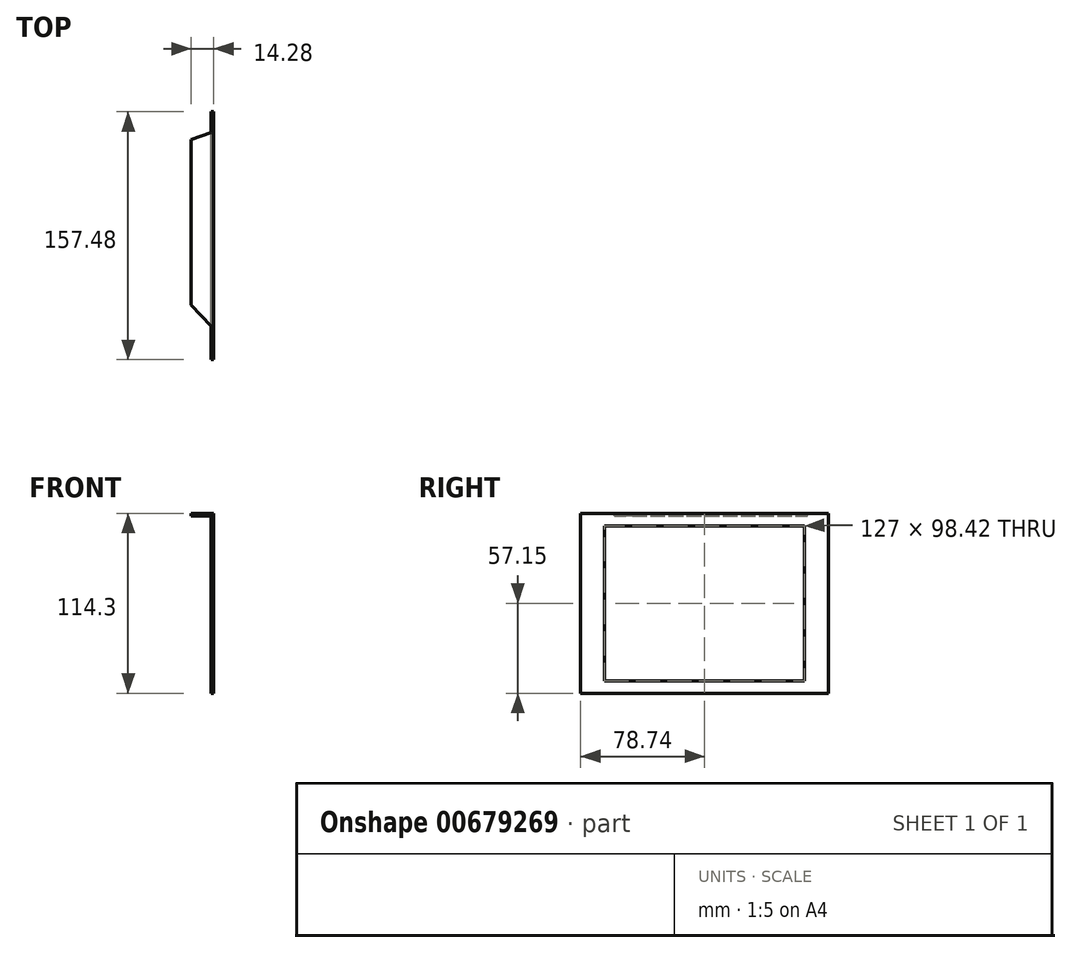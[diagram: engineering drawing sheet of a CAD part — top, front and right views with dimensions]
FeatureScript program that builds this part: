
annotation { "Feature Type Name" : "Feature", "Feature Type Description" : "" }
export const myFeature = defineFeature(function(context is Context, id is Id, definition is map)
    precondition{}
    {
        {
            var Q0;
            Q0=qCreatedBy(makeId("Top.planeOp"),FACE);
            var sketch = newSketch(context, id + "F0", { "sketchPlane" : qUnion([Q0])});
            skLineSegment(sketch, "E0.bottom", {"start": v(0.8, -78.74) * mm, "end": v(-0.8, -78.74) * mm});
            skLineSegment(sketch, "E0.top", {"start": v(0.8, 78.74) * mm, "end": v(-0.8, 78.74) * mm});
            skLineSegment(sketch, "E0.left", {"start": v(0.8, -78.74) * mm, "end": v(0.8, 78.74) * mm});
            skLineSegment(sketch, "E0.right", {"start": v(-0.8, -78.74) * mm, "end": v(-0.8, 78.74) * mm});
            skPoint(sketch, "E0.middle", {"position": v(0, 0) * mm});
            skSolve(sketch);
        }
        {
            var Q0;
            Q0=qSketchRegion(id+"F0",true);
            extrude(context, id + "F1", {"entities" : qUnion([Q0]), "depth" : 114.3 * mm});
        }
        {
            var Q0;
            Q0=makeQuery(id+"F1.opExtrude","SWEPT_FACE",FACE,{"disambiguationData":[OSD([sQuery(id+"F0.wireOp",EDGE,"E0.left")])]});
            var sketch = newSketch(context, id + "F2", { "sketchPlane" : qUnion([Q0])});
            skLineSegment(sketch, "E1.bottom", {"start": v(63.5, 106.36) * mm, "end": v(-63.5, 106.36) * mm});
            skLineSegment(sketch, "E1.top", {"start": v(63.5, 7.94) * mm, "end": v(-63.5, 7.94) * mm});
            skLineSegment(sketch, "E1.left", {"start": v(63.5, 106.36) * mm, "end": v(63.5, 7.94) * mm});
            skLineSegment(sketch, "E1.right", {"start": v(-63.5, 106.36) * mm, "end": v(-63.5, 7.94) * mm});
            skPoint(sketch, "E1.middle", {"position": v(0, 57.15) * mm});
            skPoint(sketch, "E1.middle.positionSnap0", {"position": v(-78.74, 57.15) * mm});
            skPoint(sketch, "E1.centerSnap0", {"position": v(-78.74, 57.15) * mm});
            skSolve(sketch);
        }
        {
            var Q0;
            Q0=qSketchRegion(id+"F2",true);
            extrude(context, id + "F3", {"entities" : qUnion([Q0]), "operationType" : NewBodyOperationType.REMOVE, "oppositeDirection" : true, "depth" : 25.4 * mm});
        }
        {
            var Q0;
            Q0=makeQuery(id+"F1.opExtrude","SWEPT_FACE",FACE,{"disambiguationData":[OSD([sQuery(id+"F0.wireOp",EDGE,"E0.right")])]});
            var sketch = newSketch(context, id + "F4", { "sketchPlane" : qUnion([Q0])});
            skPoint(sketch, "E2", {"position": v(-62.82, 114.3) * mm});
            skLineSegment(sketch, "E3.bottom", {"start": v(-62.82, 114.3) * mm, "end": v(54.93, 114.3) * mm});
            skLineSegment(sketch, "E3.top", {"start": v(-62.82, 112.71) * mm, "end": v(54.93, 112.71) * mm});
            skLineSegment(sketch, "E4.bottom", {"start": v(-62.82, 112.71) * mm, "end": v(-65.4, 112.71) * mm});
            skLineSegment(sketch, "E4.top", {"start": v(-62.82, 114.3) * mm, "end": v(-65.4, 114.3) * mm});
            skLineSegment(sketch, "E5.right", {"start": v(-65.4, 112.71) * mm, "end": v(-65.4, 114.3) * mm});
            skLineSegment(sketch, "E6.bottom", {"start": v(54.93, 112.71) * mm, "end": v(57.46, 112.71) * mm});
            skLineSegment(sketch, "E6.top", {"start": v(54.93, 114.3) * mm, "end": v(57.46, 114.3) * mm});
            skLineSegment(sketch, "E6.right", {"start": v(57.46, 112.71) * mm, "end": v(57.46, 114.3) * mm});
            skSolve(sketch);
        }
        {
            var Q0;
            Q0=qSketchRegion(id+"F4",true);
            extrude(context, id + "F5", {"entities" : qUnion([Q0]), "operationType" : NewBodyOperationType.ADD, "depth" : 12.7 * mm, "offsetDistance" : 25.4 * mm});
        }
        {
            var Q0;
            Q0=makeQuery(id+"F5.boolean.opBoolean","MERGE",FACE,{"derivedFrom":[makeQuery(id+"F1.opExtrude","CAP_FACE",FACE,{"disambiguationData":[OSD([sQuery(id+"F0.wireOp",EDGE,"E0.bottom"),sQuery(id+"F0.wireOp",EDGE,"E0.top"),sQuery(id+"F0.wireOp",EDGE,"E0.left"),sQuery(id+"F0.wireOp",EDGE,"E0.right")])],"isStart":false}),makeQuery(id+"F5.opExtrude","SWEPT_FACE",FACE,{"disambiguationData":[OSD([sQuery(id+"F4.wireOp",EDGE,"E3.bottom"),sQuery(id+"F4.wireOp",EDGE,"E4.top"),sQuery(id+"F4.wireOp",EDGE,"E6.top")])]})]});
            var sketch = newSketch(context, id + "F6", { "sketchPlane" : qUnion([Q0])});
            skLineSegment(sketch, "E7", {"start": v(-13.5, 65.4) * mm, "end": v(-0.8, 65.4) * mm});
            skLineSegment(sketch, "E8", {"start": v(-0.8, 65.4) * mm, "end": v(-13.5, 60.95) * mm});
            skLineSegment(sketch, "E9", {"start": v(-13.5, 60.95) * mm, "end": v(-13.5, 65.4) * mm});
            skLineSegment(sketch, "E10", {"start": v(-13.5, -57.46) * mm, "end": v(-0.8, -57.46) * mm});
            skLineSegment(sketch, "E11", {"start": v(-0.8, -57.46) * mm, "end": v(-13.5, -44.14) * mm});
            skLineSegment(sketch, "E12", {"start": v(-13.5, -44.14) * mm, "end": v(-13.5, -57.46) * mm});
            skSolve(sketch);
        }
        {
            var Q0;
            Q0 = qSketchRegion(id + "F6", true);
            extrude(context, id + "F7", {"entities" : qUnion([Q0]), "operationType" : NewBodyOperationType.REMOVE, "oppositeDirection" : true, "depth" : 25.4 * mm, "offsetDistance" : 25.4 * mm});
        }
    });
